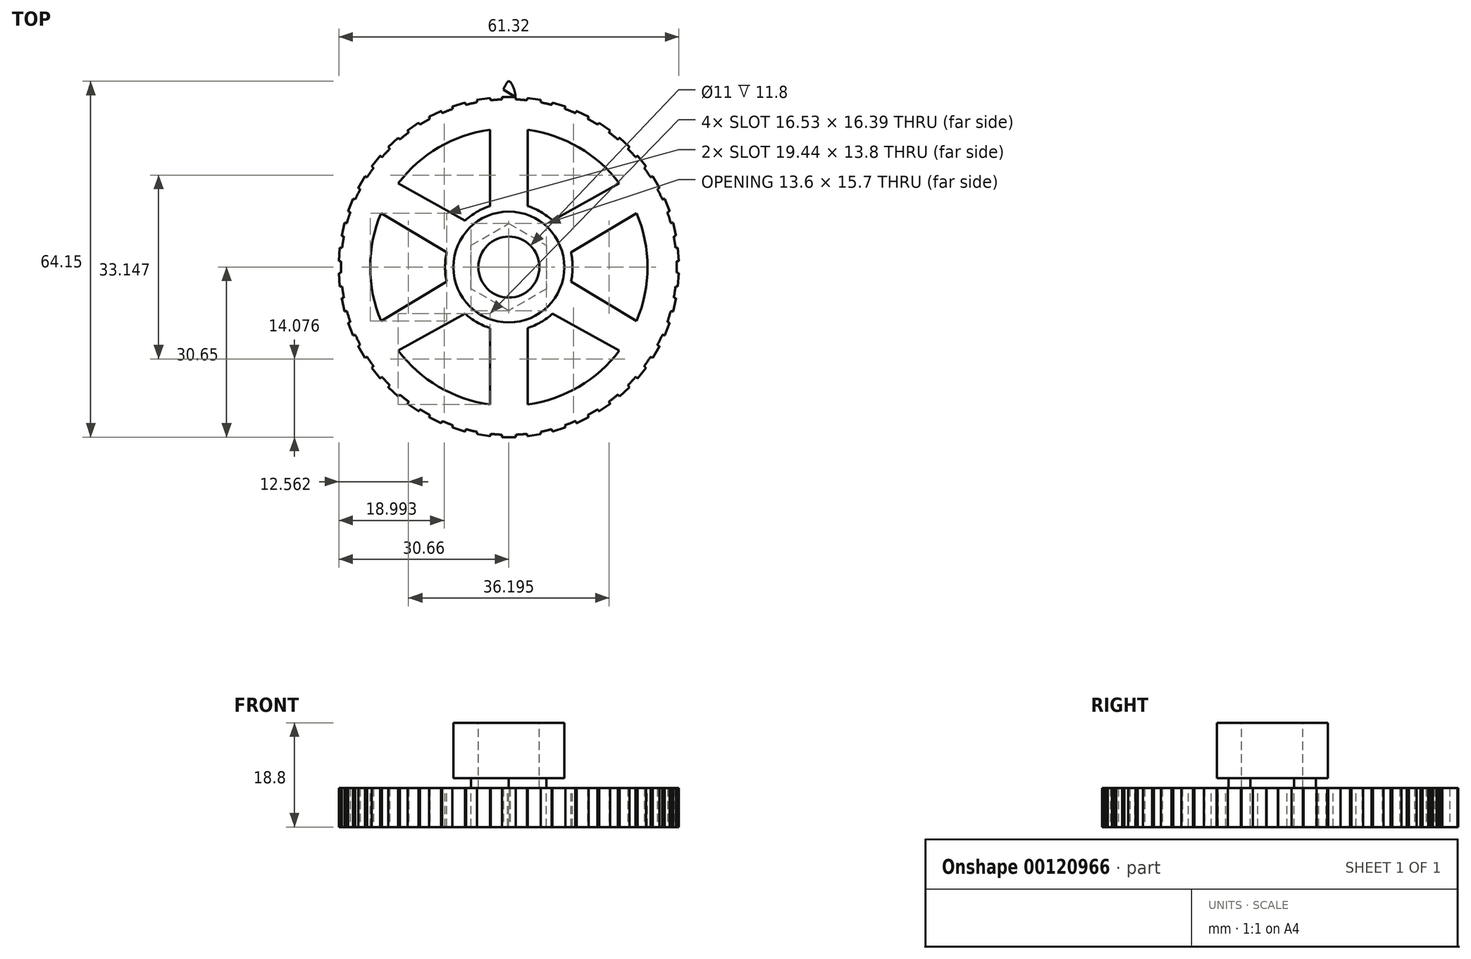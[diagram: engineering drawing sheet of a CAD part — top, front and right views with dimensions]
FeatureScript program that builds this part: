
annotation { "Feature Type Name" : "Feature", "Feature Type Description" : "" }
export const myFeature = defineFeature(function(context is Context, id is Id, definition is map)
    precondition{}
    {
        {
            var Q0;
            Q0=qCreatedBy(makeId("Top.planeOp"),FACE);
            var sketch = newSketch(context, id + "F0", { "sketchPlane" : qUnion([Q0])});
            skCircle(sketch, "E0", {"center": v(0, 0) * mm, "radius": 30 * mm});
            skCircle(sketch, "E1", {"center": v(0, 0) * mm, "radius": 33.5 * mm});
            skLineSegment(sketch, "E2", {"start": v(0, 30) * mm, "end": v(0, 33.5) * mm});
            skLineSegment(sketch, "E3", {"start": v(0, 33.5) * mm, "end": v(1.25, 33.5) * mm});
            skLineSegment(sketch, "E4", {"start": v(1.25, 33.5) * mm, "end": v(1.25, 29.64) * mm});
            skLineSegment(sketch, "E5", {"start": v(1.25, 29.64) * mm, "end": v(-1.25, 29.64) * mm});
            skLineSegment(sketch, "E6", {"start": v(-1.25, 29.64) * mm, "end": v(-1.25, 33.48) * mm});
            skLineSegment(sketch, "E7", {"start": v(-1.25, 33.48) * mm, "end": v(0, 33.5) * mm});
            skFitSpline(sketch, "E8", {"points": [v(0, 33.5) * mm, v(0.24, 33.37) * mm, v(0.97, 32) * mm, v(1.25, 29.97) * mm], "startDerivative": vector(1.35, -0.38) * mm, "endDerivative": vector(0.23, -4.54) * mm});
            skLineSegment(sketch, "E9", {"start": v(0.07, 33.48) * mm, "end": v(-0.07, 33.48) * mm});
            skLineSegment(sketch, "E10", {"start": v(-0.07, 33.48) * mm, "end": v(0.24, 33.37) * mm});
            skLineSegment(sketch, "E11", {"start": v(0.24, 33.37) * mm, "end": v(-0.24, 33.37) * mm});
            skLineSegment(sketch, "E12", {"start": v(-0.24, 33.37) * mm, "end": v(0.97, 32) * mm});
            skLineSegment(sketch, "E13", {"start": v(0.97, 32) * mm, "end": v(-0.97, 32) * mm});
            skLineSegment(sketch, "E14", {"start": v(-0.97, 32) * mm, "end": v(1.22, 30.65) * mm});
            skLineSegment(sketch, "E15", {"start": v(1.22, 30.65) * mm, "end": v(-1.21, 30.65) * mm});
            skLineSegment(sketch, "E16", {"start": v(-1.21, 30.65) * mm, "end": v(1.22, 30.65) * mm});
            skFitSpline(sketch, "E17", {"points": [v(0, 33.5) * mm, v(-0.07, 33.48) * mm, v(-0.24, 33.37) * mm, v(-0.97, 32) * mm, v(-1.21, 30.65) * mm, v(-1.25, 29.97) * mm], "startDerivative": vector(-1, -0.26) * mm, "endDerivative": vector(-0.13, -3.02) * mm});
            skSolve(sketch);
        }
        {
            var Q0;
            {var subQ0=sQuery(id+"F0.wireOp",EDGE,"E10");var subQ1=sQuery(id+"F0.wireOp",EDGE,"E2");var subQ2=makeQuery(id+"F0.imprint","INTERSECT",VERTEX,{"derivedFrom":[subQ1,subQ0]});Q0=makeQuery(id+"F0.imprint","IMPRINT",FACE,{"disambiguationData":[TD([[makeQuery(id+"F0.imprint","IMPRINT",EDGE,{"disambiguationData":[TD([[subQ2,-1.0]])],"derivedFrom":subQ1}),1.0]])]});}
            var Q1;
            {var subQ0=sQuery(id+"F0.wireOp",EDGE,"E10");var subQ1=sQuery(id+"F0.wireOp",EDGE,"E2");var subQ2=makeQuery(id+"F0.imprint","INTERSECT",VERTEX,{"derivedFrom":[subQ1,subQ0]});Q1=makeQuery(id+"F0.imprint","IMPRINT",FACE,{"disambiguationData":[TD([[makeQuery(id+"F0.imprint","IMPRINT",EDGE,{"disambiguationData":[TD([[subQ2,-1.0]])],"derivedFrom":subQ1}),-1.0]])]});}
            var Q2;
            {var subQ0=sQuery(id+"F0.wireOp",EDGE,"E11");var subQ1=sQuery(id+"F0.wireOp",EDGE,"E2");var subQ2=makeQuery(id+"F0.imprint","INTERSECT",VERTEX,{"derivedFrom":[subQ1,subQ0]});Q2=makeQuery(id+"F0.imprint","IMPRINT",FACE,{"disambiguationData":[TD([[makeQuery(id+"F0.imprint","IMPRINT",EDGE,{"disambiguationData":[TD([[subQ2,-1.0]])],"derivedFrom":subQ1}),-1.0]])]});}
            var Q3;
            {var subQ0=sQuery(id+"F0.wireOp",EDGE,"E11");var subQ1=sQuery(id+"F0.wireOp",EDGE,"E2");var subQ2=makeQuery(id+"F0.imprint","INTERSECT",VERTEX,{"derivedFrom":[subQ1,subQ0]});Q3=makeQuery(id+"F0.imprint","IMPRINT",FACE,{"disambiguationData":[TD([[makeQuery(id+"F0.imprint","IMPRINT",EDGE,{"disambiguationData":[TD([[subQ2,-1.0]])],"derivedFrom":subQ1}),1.0]])]});}
            var Q4;
            {var subQ0=sQuery(id+"F0.wireOp",EDGE,"E12");var subQ1=sQuery(id+"F0.wireOp",EDGE,"E2");var subQ2=makeQuery(id+"F0.imprint","INTERSECT",VERTEX,{"derivedFrom":[subQ1,subQ0]});Q4=makeQuery(id+"F0.imprint","IMPRINT",FACE,{"disambiguationData":[TD([[makeQuery(id+"F0.imprint","IMPRINT",EDGE,{"disambiguationData":[TD([[subQ2,-1.0]])],"derivedFrom":subQ1}),1.0]])]});}
            var Q5;
            {var subQ0=sQuery(id+"F0.wireOp",EDGE,"E12");var subQ1=sQuery(id+"F0.wireOp",EDGE,"E2");var subQ2=makeQuery(id+"F0.imprint","INTERSECT",VERTEX,{"derivedFrom":[subQ1,subQ0]});Q5=makeQuery(id+"F0.imprint","IMPRINT",FACE,{"disambiguationData":[TD([[makeQuery(id+"F0.imprint","IMPRINT",EDGE,{"disambiguationData":[TD([[subQ2,-1.0]])],"derivedFrom":subQ1}),-1.0]])]});}
            var Q6;
            {var subQ0=sQuery(id+"F0.wireOp",EDGE,"E13");var subQ1=sQuery(id+"F0.wireOp",EDGE,"E2");var subQ2=makeQuery(id+"F0.imprint","INTERSECT",VERTEX,{"derivedFrom":[subQ1,subQ0]});Q6=makeQuery(id+"F0.imprint","IMPRINT",FACE,{"disambiguationData":[TD([[makeQuery(id+"F0.imprint","IMPRINT",EDGE,{"disambiguationData":[TD([[subQ2,-1.0]])],"derivedFrom":subQ1}),1.0]])]});}
            var Q7;
            {var subQ0=sQuery(id+"F0.wireOp",EDGE,"E13");var subQ1=sQuery(id+"F0.wireOp",EDGE,"E2");var subQ2=makeQuery(id+"F0.imprint","INTERSECT",VERTEX,{"derivedFrom":[subQ1,subQ0]});Q7=makeQuery(id+"F0.imprint","IMPRINT",FACE,{"disambiguationData":[TD([[makeQuery(id+"F0.imprint","IMPRINT",EDGE,{"disambiguationData":[TD([[subQ2,-1.0]])],"derivedFrom":subQ1}),-1.0]])]});}
            var Q8;
            {var subQ0=sQuery(id+"F0.wireOp",EDGE,"E14");var subQ1=sQuery(id+"F0.wireOp",EDGE,"E2");var subQ2=makeQuery(id+"F0.imprint","INTERSECT",VERTEX,{"derivedFrom":[subQ1,subQ0]});Q8=makeQuery(id+"F0.imprint","IMPRINT",FACE,{"disambiguationData":[TD([[makeQuery(id+"F0.imprint","IMPRINT",EDGE,{"disambiguationData":[TD([[subQ2,-1.0]])],"derivedFrom":subQ1}),-1.0]])]});}
            var Q9;
            {var subQ0=sQuery(id+"F0.wireOp",EDGE,"E14");var subQ1=sQuery(id+"F0.wireOp",EDGE,"E2");var subQ2=makeQuery(id+"F0.imprint","INTERSECT",VERTEX,{"derivedFrom":[subQ1,subQ0]});Q9=makeQuery(id+"F0.imprint","IMPRINT",FACE,{"disambiguationData":[TD([[makeQuery(id+"F0.imprint","IMPRINT",EDGE,{"disambiguationData":[TD([[subQ2,-1.0]])],"derivedFrom":subQ1}),1.0]])]});}
            var Q10;
            {var subQ0=sQuery(id+"F0.wireOp",EDGE,"E16");var subQ1=sQuery(id+"F0.wireOp",EDGE,"E2");var subQ2=makeQuery(id+"F0.imprint","INTERSECT",VERTEX,{"derivedFrom":[subQ1,subQ0]});Q10=makeQuery(id+"F0.imprint","IMPRINT",FACE,{"disambiguationData":[TD([[makeQuery(id+"F0.imprint","IMPRINT",EDGE,{"disambiguationData":[TD([[subQ2,-1.0]])],"derivedFrom":subQ1}),1.0]])]});}
            var Q11;
            {var subQ0=sQuery(id+"F0.wireOp",EDGE,"E16");var subQ1=sQuery(id+"F0.wireOp",EDGE,"E2");var subQ2=makeQuery(id+"F0.imprint","INTERSECT",VERTEX,{"derivedFrom":[subQ1,subQ0]});Q11=makeQuery(id+"F0.imprint","IMPRINT",FACE,{"disambiguationData":[TD([[makeQuery(id+"F0.imprint","IMPRINT",EDGE,{"disambiguationData":[TD([[subQ2,-1.0]])],"derivedFrom":subQ1}),-1.0]])]});}
            var Q12;
            {var subQ0=sQuery(id+"F0.wireOp",EDGE,"E2");var subQ1=sQuery(id+"F0.wireOp",EDGE,"E0");var subQ2=makeQuery(id+"F0.imprint","INTERSECT",VERTEX,{"derivedFrom":[subQ1,subQ0]});Q12=makeQuery(id+"F0.imprint","IMPRINT",FACE,{"disambiguationData":[TD([[makeQuery(id+"F0.imprint","IMPRINT",EDGE,{"disambiguationData":[TD([[subQ2,-1.0]])],"derivedFrom":subQ0}),-1.0]])]});}
            var Q13;
            {var subQ0=sQuery(id+"F0.wireOp",EDGE,"E2");var subQ1=sQuery(id+"F0.wireOp",EDGE,"E0");var subQ2=makeQuery(id+"F0.imprint","INTERSECT",VERTEX,{"derivedFrom":[subQ1,subQ0]});Q13=makeQuery(id+"F0.imprint","IMPRINT",FACE,{"disambiguationData":[TD([[makeQuery(id+"F0.imprint","IMPRINT",EDGE,{"disambiguationData":[TD([[subQ2,-1.0]])],"derivedFrom":subQ0}),1.0]])]});}
            extrude(context, id + "F1", {"entities" : qUnion([Q0, Q1, Q2, Q3, Q4, Q5, Q6, Q7, Q8, Q9, Q10, Q11, Q12, Q13]), "depth" : 7 * mm});
        }
        {
            var Q0;
            Q0=qCreatedBy(makeId("Top.planeOp"),FACE);
            var sketch = newSketch(context, id + "F2", { "sketchPlane" : qUnion([Q0])});
            skCircle(sketch, "E18", {"center": v(0, 0) * mm, "radius": 4.18 * mm});
            skSolve(sketch);
        }
        {
            var Q0;
            Q0 = qSketchRegion(id + "F2", true);
            extrude(context, id + "F3", {"entities" : qUnion([Q0]), "depth" : 25 * mm});
        }
        {
            var Q0;
            Q0=makeQuery(id+"F1.opExtrude","SWEPT_BODY",BODY,{"disambiguationData":[OSD([sQuery(id+"F0.wireOp",EDGE,"E0"),sQuery(id+"F0.wireOp",EDGE,"E8"),sQuery(id+"F0.wireOp",EDGE,"E9"),sQuery(id+"F0.wireOp",EDGE,"E17")])]});
            var Q1;
            Q1=makeQuery(id+"F3.opExtrude","CAP_EDGE",EDGE,{"disambiguationData":[OSD([sQuery(id+"F2.wireOp",EDGE,"E18")])],"isStart":false});
            circularPattern(context, id + "F4", {"entities" : qUnion([Q0]), "axis" : qUnion([Q1]), "angle" : 360 * degree, "instanceCount" : 42, "equalSpace" : true});
        }
        {
            var Q0;
            Q0=makeQuery(id+"F3.opExtrude","CAP_FACE",FACE,{"disambiguationData":[OSD([sQuery(id+"F2.wireOp",EDGE,"E18")])],"isStart":false});
            var sketch = newSketch(context, id + "F5", { "sketchPlane" : qUnion([Q0])});
            skCircle(sketch, "E19", {"center": v(0, 0) * mm, "radius": 6.48 * mm});
            skSolve(sketch);
        }
        {
            var Q0;
            Q0 = qSketchRegion(id + "F5", true);
            extrude(context, id + "F6", {"entities" : qUnion([Q0]), "operationType" : NewBodyOperationType.REMOVE, "oppositeDirection" : true, "depth" : 25 * mm});
        }
        {
            var Q0;
            Q0=qCreatedBy(makeId("Top.planeOp"),FACE);
            var sketch = newSketch(context, id + "F7", { "sketchPlane" : qUnion([Q0])});
            skCircle(sketch, "E20", {"center": v(0, 0) * mm, "radius": 30.25 * mm});
            skSolve(sketch);
        }
        {
            var Q0;
            Q0=makeQuery(id+"F7.imprint","IMPRINT",FACE,{"disambiguationData":[TD([[makeQuery(id+"F7.imprint","IMPRINT",EDGE,{"derivedFrom":sQuery(id+"F7.wireOp",EDGE,"E20")}),1.0]])]});
            extrude(context, id + "F8", {"entities" : qUnion([Q0]), "operationType" : NewBodyOperationType.ADD, "depth" : 7 * mm});
        }
        {
            var Q0;
            {var subQ0=makeQuery(id+"F1.opExtrude","CAP_FACE",FACE,{"disambiguationData":[OSD([sQuery(id+"F0.wireOp",EDGE,"E0"),sQuery(id+"F0.wireOp",EDGE,"E8"),sQuery(id+"F0.wireOp",EDGE,"E9"),sQuery(id+"F0.wireOp",EDGE,"E17")])],"isStart":false});Q0=makeQuery(id+"F8.boolean.opBoolean","MERGE",FACE,{"derivedFrom":[subQ0,makeQuery(id+"F4.opPattern","COPY",FACE,{"derivedFrom":subQ0,"instanceName":"1"}),makeQuery(id+"F4.opPattern","COPY",FACE,{"derivedFrom":subQ0,"instanceName":"2"}),makeQuery(id+"F4.opPattern","COPY",FACE,{"derivedFrom":subQ0,"instanceName":"3"}),makeQuery(id+"F4.opPattern","COPY",FACE,{"derivedFrom":subQ0,"instanceName":"4"}),makeQuery(id+"F4.opPattern","COPY",FACE,{"derivedFrom":subQ0,"instanceName":"5"}),makeQuery(id+"F4.opPattern","COPY",FACE,{"derivedFrom":subQ0,"instanceName":"6"}),makeQuery(id+"F4.opPattern","COPY",FACE,{"derivedFrom":subQ0,"instanceName":"7"}),makeQuery(id+"F4.opPattern","COPY",FACE,{"derivedFrom":subQ0,"instanceName":"8"}),makeQuery(id+"F4.opPattern","COPY",FACE,{"derivedFrom":subQ0,"instanceName":"9"}),makeQuery(id+"F4.opPattern","COPY",FACE,{"derivedFrom":subQ0,"instanceName":"10"}),makeQuery(id+"F4.opPattern","COPY",FACE,{"derivedFrom":subQ0,"instanceName":"11"}),makeQuery(id+"F4.opPattern","COPY",FACE,{"derivedFrom":subQ0,"instanceName":"12"}),makeQuery(id+"F4.opPattern","COPY",FACE,{"derivedFrom":subQ0,"instanceName":"13"}),makeQuery(id+"F4.opPattern","COPY",FACE,{"derivedFrom":subQ0,"instanceName":"14"}),makeQuery(id+"F4.opPattern","COPY",FACE,{"derivedFrom":subQ0,"instanceName":"15"}),makeQuery(id+"F4.opPattern","COPY",FACE,{"derivedFrom":subQ0,"instanceName":"16"}),makeQuery(id+"F4.opPattern","COPY",FACE,{"derivedFrom":subQ0,"instanceName":"17"}),makeQuery(id+"F4.opPattern","COPY",FACE,{"derivedFrom":subQ0,"instanceName":"18"}),makeQuery(id+"F4.opPattern","COPY",FACE,{"derivedFrom":subQ0,"instanceName":"19"}),makeQuery(id+"F4.opPattern","COPY",FACE,{"derivedFrom":subQ0,"instanceName":"20"}),makeQuery(id+"F4.opPattern","COPY",FACE,{"derivedFrom":subQ0,"instanceName":"21"}),makeQuery(id+"F4.opPattern","COPY",FACE,{"derivedFrom":subQ0,"instanceName":"22"}),makeQuery(id+"F4.opPattern","COPY",FACE,{"derivedFrom":subQ0,"instanceName":"23"}),makeQuery(id+"F4.opPattern","COPY",FACE,{"derivedFrom":subQ0,"instanceName":"24"}),makeQuery(id+"F4.opPattern","COPY",FACE,{"derivedFrom":subQ0,"instanceName":"25"}),makeQuery(id+"F4.opPattern","COPY",FACE,{"derivedFrom":subQ0,"instanceName":"26"}),makeQuery(id+"F4.opPattern","COPY",FACE,{"derivedFrom":subQ0,"instanceName":"27"}),makeQuery(id+"F4.opPattern","COPY",FACE,{"derivedFrom":subQ0,"instanceName":"28"}),makeQuery(id+"F4.opPattern","COPY",FACE,{"derivedFrom":subQ0,"instanceName":"29"}),makeQuery(id+"F4.opPattern","COPY",FACE,{"derivedFrom":subQ0,"instanceName":"30"}),makeQuery(id+"F4.opPattern","COPY",FACE,{"derivedFrom":subQ0,"instanceName":"31"}),makeQuery(id+"F4.opPattern","COPY",FACE,{"derivedFrom":subQ0,"instanceName":"32"}),makeQuery(id+"F4.opPattern","COPY",FACE,{"derivedFrom":subQ0,"instanceName":"33"}),makeQuery(id+"F4.opPattern","COPY",FACE,{"derivedFrom":subQ0,"instanceName":"34"}),makeQuery(id+"F4.opPattern","COPY",FACE,{"derivedFrom":subQ0,"instanceName":"35"}),makeQuery(id+"F4.opPattern","COPY",FACE,{"derivedFrom":subQ0,"instanceName":"36"}),makeQuery(id+"F4.opPattern","COPY",FACE,{"derivedFrom":subQ0,"instanceName":"37"}),makeQuery(id+"F4.opPattern","COPY",FACE,{"derivedFrom":subQ0,"instanceName":"38"}),makeQuery(id+"F4.opPattern","COPY",FACE,{"derivedFrom":subQ0,"instanceName":"39"}),makeQuery(id+"F4.opPattern","COPY",FACE,{"derivedFrom":subQ0,"instanceName":"40"}),makeQuery(id+"F4.opPattern","COPY",FACE,{"derivedFrom":subQ0,"instanceName":"41"}),makeQuery(id+"F4.opPattern","COPY",FACE,{"derivedFrom":subQ0,"instanceName":"42"}),makeQuery(id+"F4.opPattern","COPY",FACE,{"derivedFrom":subQ0,"instanceName":"43"}),makeQuery(id+"F4.opPattern","COPY",FACE,{"derivedFrom":subQ0,"instanceName":"44"}),makeQuery(id+"F4.opPattern","COPY",FACE,{"derivedFrom":subQ0,"instanceName":"45"}),makeQuery(id+"F4.opPattern","COPY",FACE,{"derivedFrom":subQ0,"instanceName":"46"}),makeQuery(id+"F4.opPattern","COPY",FACE,{"derivedFrom":subQ0,"instanceName":"47"}),makeQuery(id+"F4.opPattern","COPY",FACE,{"derivedFrom":subQ0,"instanceName":"48"}),makeQuery(id+"F4.opPattern","COPY",FACE,{"derivedFrom":subQ0,"instanceName":"49"}),makeQuery(id+"F4.opPattern","COPY",FACE,{"derivedFrom":subQ0,"instanceName":"50"}),makeQuery(id+"F4.opPattern","COPY",FACE,{"derivedFrom":subQ0,"instanceName":"51"}),makeQuery(id+"F4.opPattern","COPY",FACE,{"derivedFrom":subQ0,"instanceName":"52"}),makeQuery(id+"F4.opPattern","COPY",FACE,{"derivedFrom":subQ0,"instanceName":"53"}),makeQuery(id+"F8.opExtrude","CAP_FACE",FACE,{"disambiguationData":[OSD([sQuery(id+"F7.wireOp",EDGE,"E20")])],"isStart":false})]});}
            var sketch = newSketch(context, id + "F9", { "sketchPlane" : qUnion([Q0])});
            skLineSegment(sketch, "E21", {"start": v(0, 0) * mm, "end": v(6.8, 0) * mm});
            skCircle(sketch, "E22.cCircle", {"center": v(0, 0) * mm, "radius": 6.8 * mm, "construction": true});
            skLineSegment(sketch, "E22.0", {"start": v(6.8, 3.93) * mm, "end": v(6.8, -3.93) * mm});
            skLineSegment(sketch, "E22.1", {"start": v(6.8, -3.93) * mm, "end": v(0, -7.85) * mm});
            skLineSegment(sketch, "E22.2", {"start": v(0, -7.85) * mm, "end": v(-6.8, -3.93) * mm});
            skLineSegment(sketch, "E22.3", {"start": v(-6.8, -3.93) * mm, "end": v(-6.8, 3.93) * mm});
            skLineSegment(sketch, "E22.4", {"start": v(-6.8, 3.93) * mm, "end": v(0, 7.85) * mm});
            skLineSegment(sketch, "E22.5", {"start": v(0, 7.85) * mm, "end": v(6.8, 3.93) * mm});
            skPoint(sketch, "E22.0.midPoint", {"position": v(6.8, 0) * mm});
            skCircle(sketch, "E23", {"center": v(0, 0) * mm, "radius": 25 * mm});
            skCircle(sketch, "E24.cCircle", {"center": v(0, 0) * mm, "radius": 25.74 * mm, "construction": true});
            skCircle(sketch, "E25", {"center": v(0, 0) * mm, "radius": 11.5 * mm});
            skLineSegment(sketch, "E26", {"start": v(6.8, 0) * mm, "end": v(23.67, 10.1) * mm});
            skLineSegment(sketch, "E27", {"start": v(3.4, 5.89) * mm, "end": v(20.58, 15.45) * mm});
            skLineSegment(sketch, "E28", {"start": v(3.4, 5.89) * mm, "end": v(3.4, 25.51) * mm});
            skLineSegment(sketch, "E29", {"start": v(-3.4, 5.89) * mm, "end": v(-3.4, 25.51) * mm});
            skLineSegment(sketch, "E30", {"start": v(-3.4, -5.89) * mm, "end": v(-3.4, -25.51) * mm});
            skLineSegment(sketch, "E31", {"start": v(3.4, -5.89) * mm, "end": v(3.4, -25.51) * mm});
            skLineSegment(sketch, "E32", {"start": v(3.4, -5.89) * mm, "end": v(20.58, -15.45) * mm});
            skLineSegment(sketch, "E33", {"start": v(6.8, 0) * mm, "end": v(23.67, -10.1) * mm});
            skLineSegment(sketch, "E34", {"start": v(-3.4, -5.89) * mm, "end": v(-20.58, -15.45) * mm});
            skLineSegment(sketch, "E35", {"start": v(-6.8, 0) * mm, "end": v(-23.67, -10.1) * mm});
            skLineSegment(sketch, "E36", {"start": v(-3.4, 5.89) * mm, "end": v(-20.58, 15.45) * mm});
            skLineSegment(sketch, "E37", {"start": v(-6.8, 0) * mm, "end": v(-23.67, 10.1) * mm});
            skSolve(sketch);
        }
        {
            var Q0;
            {var subQ0=sQuery(id+"F9.wireOp",EDGE,"E27");var subQ1=sQuery(id+"F9.wireOp",EDGE,"E23");var subQ2=makeQuery(id+"F9.imprint","INTERSECT",VERTEX,{"derivedFrom":[subQ1,subQ0]});Q0=makeQuery(id+"F9.imprint","IMPRINT",FACE,{"disambiguationData":[TD([[makeQuery(id+"F9.imprint","IMPRINT",EDGE,{"disambiguationData":[TD([[subQ2,-1.0]])],"derivedFrom":subQ1}),1.0]])]});}
            var Q1;
            {var subQ0=sQuery(id+"F9.wireOp",EDGE,"E29");var subQ1=sQuery(id+"F9.wireOp",EDGE,"E23");var subQ2=makeQuery(id+"F9.imprint","INTERSECT",VERTEX,{"derivedFrom":[subQ1,subQ0]});Q1=makeQuery(id+"F9.imprint","IMPRINT",FACE,{"disambiguationData":[TD([[makeQuery(id+"F9.imprint","IMPRINT",EDGE,{"disambiguationData":[TD([[subQ2,-1.0]])],"derivedFrom":subQ1}),1.0]])]});}
            var Q2;
            {var subQ0=sQuery(id+"F9.wireOp",EDGE,"E35");var subQ1=sQuery(id+"F9.wireOp",EDGE,"E23");var subQ2=makeQuery(id+"F9.imprint","INTERSECT",VERTEX,{"derivedFrom":[subQ1,subQ0]});Q2=makeQuery(id+"F9.imprint","IMPRINT",FACE,{"disambiguationData":[TD([[makeQuery(id+"F9.imprint","IMPRINT",EDGE,{"disambiguationData":[TD([[subQ2,1.0]])],"derivedFrom":subQ1}),1.0]])]});}
            var Q3;
            {var subQ0=sQuery(id+"F9.wireOp",EDGE,"E30");var subQ1=sQuery(id+"F9.wireOp",EDGE,"E23");var subQ2=makeQuery(id+"F9.imprint","INTERSECT",VERTEX,{"derivedFrom":[subQ1,subQ0]});Q3=makeQuery(id+"F9.imprint","IMPRINT",FACE,{"disambiguationData":[TD([[makeQuery(id+"F9.imprint","IMPRINT",EDGE,{"disambiguationData":[TD([[subQ2,1.0]])],"derivedFrom":subQ1}),1.0]])]});}
            var Q4;
            {var subQ0=sQuery(id+"F9.wireOp",EDGE,"E31");var subQ1=sQuery(id+"F9.wireOp",EDGE,"E23");var subQ2=makeQuery(id+"F9.imprint","INTERSECT",VERTEX,{"derivedFrom":[subQ1,subQ0]});Q4=makeQuery(id+"F9.imprint","IMPRINT",FACE,{"disambiguationData":[TD([[makeQuery(id+"F9.imprint","IMPRINT",EDGE,{"disambiguationData":[TD([[subQ2,-1.0]])],"derivedFrom":subQ1}),1.0]])]});}
            var Q5;
            {var subQ0=sQuery(id+"F9.wireOp",EDGE,"E22.5");var subQ11=sQuery(id+"F9.wireOp",EDGE,"E22.0");var subQ16=makeQuery(id+"F9.imprint","INTERSECT",VERTEX,{"derivedFrom":[subQ11,subQ0]});Q5=makeQuery(id+"F9.imprint","IMPRINT",FACE,{"disambiguationData":[TD([[makeQuery(id+"F9.imprint","IMPRINT",EDGE,{"disambiguationData":[TD([[subQ16,-1.0]])],"derivedFrom":subQ11}),-1.0]])]});}
            var Q6;
            {var subQ0=sQuery(id+"F9.wireOp",EDGE,"E26");var subQ1=sQuery(id+"F9.wireOp",EDGE,"E23");var subQ2=makeQuery(id+"F9.imprint","INTERSECT",VERTEX,{"derivedFrom":[subQ1,subQ0]});Q6=makeQuery(id+"F9.imprint","IMPRINT",FACE,{"disambiguationData":[TD([[makeQuery(id+"F9.imprint","IMPRINT",EDGE,{"disambiguationData":[TD([[subQ2,1.0]])],"derivedFrom":subQ1}),1.0]])]});}
            extrude(context, id + "F10", {"entities" : qUnion([Q0, Q1, Q2, Q3, Q4, Q5, Q6]), "operationType" : NewBodyOperationType.REMOVE, "oppositeDirection" : true, "depth" : 25 * mm});
        }
        {
            var Q0;
            {var subQ0=makeQuery(id+"F1.opExtrude","CAP_FACE",FACE,{"disambiguationData":[OSD([sQuery(id+"F0.wireOp",EDGE,"E0"),sQuery(id+"F0.wireOp",EDGE,"E8"),sQuery(id+"F0.wireOp",EDGE,"E9"),sQuery(id+"F0.wireOp",EDGE,"E17")])],"isStart":false});Q0=makeQuery(id+"F8.boolean.opBoolean","MERGE",FACE,{"derivedFrom":[subQ0,makeQuery(id+"F4.opPattern","COPY",FACE,{"derivedFrom":subQ0,"instanceName":"1"}),makeQuery(id+"F4.opPattern","COPY",FACE,{"derivedFrom":subQ0,"instanceName":"2"}),makeQuery(id+"F4.opPattern","COPY",FACE,{"derivedFrom":subQ0,"instanceName":"3"}),makeQuery(id+"F4.opPattern","COPY",FACE,{"derivedFrom":subQ0,"instanceName":"4"}),makeQuery(id+"F4.opPattern","COPY",FACE,{"derivedFrom":subQ0,"instanceName":"5"}),makeQuery(id+"F4.opPattern","COPY",FACE,{"derivedFrom":subQ0,"instanceName":"6"}),makeQuery(id+"F4.opPattern","COPY",FACE,{"derivedFrom":subQ0,"instanceName":"7"}),makeQuery(id+"F4.opPattern","COPY",FACE,{"derivedFrom":subQ0,"instanceName":"8"}),makeQuery(id+"F4.opPattern","COPY",FACE,{"derivedFrom":subQ0,"instanceName":"9"}),makeQuery(id+"F4.opPattern","COPY",FACE,{"derivedFrom":subQ0,"instanceName":"10"}),makeQuery(id+"F4.opPattern","COPY",FACE,{"derivedFrom":subQ0,"instanceName":"11"}),makeQuery(id+"F4.opPattern","COPY",FACE,{"derivedFrom":subQ0,"instanceName":"12"}),makeQuery(id+"F4.opPattern","COPY",FACE,{"derivedFrom":subQ0,"instanceName":"13"}),makeQuery(id+"F4.opPattern","COPY",FACE,{"derivedFrom":subQ0,"instanceName":"14"}),makeQuery(id+"F4.opPattern","COPY",FACE,{"derivedFrom":subQ0,"instanceName":"15"}),makeQuery(id+"F4.opPattern","COPY",FACE,{"derivedFrom":subQ0,"instanceName":"16"}),makeQuery(id+"F4.opPattern","COPY",FACE,{"derivedFrom":subQ0,"instanceName":"17"}),makeQuery(id+"F4.opPattern","COPY",FACE,{"derivedFrom":subQ0,"instanceName":"18"}),makeQuery(id+"F4.opPattern","COPY",FACE,{"derivedFrom":subQ0,"instanceName":"19"}),makeQuery(id+"F4.opPattern","COPY",FACE,{"derivedFrom":subQ0,"instanceName":"20"}),makeQuery(id+"F4.opPattern","COPY",FACE,{"derivedFrom":subQ0,"instanceName":"21"}),makeQuery(id+"F4.opPattern","COPY",FACE,{"derivedFrom":subQ0,"instanceName":"22"}),makeQuery(id+"F4.opPattern","COPY",FACE,{"derivedFrom":subQ0,"instanceName":"23"}),makeQuery(id+"F4.opPattern","COPY",FACE,{"derivedFrom":subQ0,"instanceName":"24"}),makeQuery(id+"F4.opPattern","COPY",FACE,{"derivedFrom":subQ0,"instanceName":"25"}),makeQuery(id+"F4.opPattern","COPY",FACE,{"derivedFrom":subQ0,"instanceName":"26"}),makeQuery(id+"F4.opPattern","COPY",FACE,{"derivedFrom":subQ0,"instanceName":"27"}),makeQuery(id+"F4.opPattern","COPY",FACE,{"derivedFrom":subQ0,"instanceName":"28"}),makeQuery(id+"F4.opPattern","COPY",FACE,{"derivedFrom":subQ0,"instanceName":"29"}),makeQuery(id+"F4.opPattern","COPY",FACE,{"derivedFrom":subQ0,"instanceName":"30"}),makeQuery(id+"F4.opPattern","COPY",FACE,{"derivedFrom":subQ0,"instanceName":"31"}),makeQuery(id+"F4.opPattern","COPY",FACE,{"derivedFrom":subQ0,"instanceName":"32"}),makeQuery(id+"F4.opPattern","COPY",FACE,{"derivedFrom":subQ0,"instanceName":"33"}),makeQuery(id+"F4.opPattern","COPY",FACE,{"derivedFrom":subQ0,"instanceName":"34"}),makeQuery(id+"F4.opPattern","COPY",FACE,{"derivedFrom":subQ0,"instanceName":"35"}),makeQuery(id+"F4.opPattern","COPY",FACE,{"derivedFrom":subQ0,"instanceName":"36"}),makeQuery(id+"F4.opPattern","COPY",FACE,{"derivedFrom":subQ0,"instanceName":"37"}),makeQuery(id+"F4.opPattern","COPY",FACE,{"derivedFrom":subQ0,"instanceName":"38"}),makeQuery(id+"F4.opPattern","COPY",FACE,{"derivedFrom":subQ0,"instanceName":"39"}),makeQuery(id+"F4.opPattern","COPY",FACE,{"derivedFrom":subQ0,"instanceName":"40"}),makeQuery(id+"F4.opPattern","COPY",FACE,{"derivedFrom":subQ0,"instanceName":"41"}),makeQuery(id+"F8.opExtrude","CAP_FACE",FACE,{"disambiguationData":[OSD([sQuery(id+"F7.wireOp",EDGE,"E20")])],"isStart":false})]});}
            var sketch = newSketch(context, id + "F11", { "sketchPlane" : qUnion([Q0])});
            skCircle(sketch, "E38", {"center": v(0, 0) * mm, "radius": 11.5 * mm});
            skCircle(sketch, "E39", {"center": v(0, 0) * mm, "radius": 5 * mm});
            skSolve(sketch);
        }
        {
            var Q0;
            Q0=makeQuery(id+"F11.imprint","IMPRINT",FACE,{"disambiguationData":[TD([[makeQuery(id+"F11.imprint","IMPRINT",EDGE,{"derivedFrom":makeQuery(id+"F10.boolean.opBoolean","COPY",EDGE,{"derivedFrom":makeQuery(id+"F10.opExtrude","CAP_EDGE",EDGE,{"disambiguationData":[OSD([sQuery(id+"F9.wireOp",EDGE,"E22.0")])],"isStart":true})})}),1.0]])]});
            var Q1;
            Q1=makeQuery(id+"F11.imprint","IMPRINT",FACE,{"disambiguationData":[TD([[makeQuery(id+"F11.imprint","IMPRINT",EDGE,{"derivedFrom":sQuery(id+"F11.wireOp",EDGE,"E39")}),-1.0]])]});
            extrude(context, id + "F12", {"entities" : qUnion([Q0, Q1]), "operationType" : NewBodyOperationType.ADD, "depth" : 1.8 * mm});
        }
        {
            var Q0;
            Q0=makeQuery(id+"F12.opExtrude","CAP_FACE",FACE,{"disambiguationData":[OSD([sQuery(id+"F11.wireOp",EDGE,"E38"),sQuery(id+"F11.wireOp",EDGE,"E39")])],"isStart":false});
            var sketch = newSketch(context, id + "F13", { "sketchPlane" : qUnion([Q0])});
            skCircle(sketch, "E40", {"center": v(0, 0) * mm, "radius": 5.02 * mm});
            skCircle(sketch, "E41", {"center": v(0, 0) * mm, "radius": 9.9 * mm});
            skSolve(sketch);
        }
        {
            var Q0;
            Q0=makeQuery(id+"F13.imprint","IMPRINT",FACE,{"disambiguationData":[TD([[makeQuery(id+"F13.imprint","IMPRINT",EDGE,{"derivedFrom":sQuery(id+"F13.wireOp",EDGE,"E40")}),-1.0]])]});
            extrude(context, id + "F14", {"entities" : qUnion([Q0]), "operationType" : NewBodyOperationType.ADD, "depth" : 10 * mm});
        }
        {
            var Q0;
            {var subQ1=sQuery(id+"F11.wireOp",EDGE,"E38");Q0=makeQuery(id+"F14.boolean.opBoolean","SPLIT",FACE,{"disambiguationData":[TD([makeQuery(id+"F12.opExtrude","SWEPT_FACE",FACE,{"disambiguationData":[OSD([subQ1])]})])],"derivedFrom":makeQuery(id+"F12.opExtrude","CAP_FACE",FACE,{"disambiguationData":[OSD([subQ1,sQuery(id+"F11.wireOp",EDGE,"E39")])],"isStart":false})});}
            var sketch = newSketch(context, id + "F15", { "sketchPlane" : qUnion([Q0])});
            skCircle(sketch, "E42", {"center": v(0, 0) * mm, "radius": 10.7 * mm});
            skSolve(sketch);
        }
        {
            var Q0;
            Q0=makeQuery(id+"F15.imprint","IMPRINT",FACE,{"disambiguationData":[TD([[makeQuery(id+"F15.imprint","IMPRINT",EDGE,{"derivedFrom":sQuery(id+"F15.wireOp",EDGE,"E42")}),1.0]])]});
            extrude(context, id + "F16", {"entities" : qUnion([Q0]), "operationType" : NewBodyOperationType.ADD, "depth" : 10 * mm});
        }
        {
            var Q0;
            {var subQ0=sQuery(id+"F13.wireOp",EDGE,"E41");Q0=makeQuery(id+"F16.boolean.opBoolean","MERGE",FACE,{"derivedFrom":[makeQuery(id+"F14.opExtrude","CAP_FACE",FACE,{"disambiguationData":[OSD([sQuery(id+"F13.wireOp",EDGE,"E40"),subQ0])],"isStart":false}),makeQuery(id+"F16.opExtrude","CAP_FACE",FACE,{"disambiguationData":[OSD([subQ0,sQuery(id+"F15.wireOp",EDGE,"E42")])],"isStart":false})]});}
            var sketch = newSketch(context, id + "F17", { "sketchPlane" : qUnion([Q0])});
            skCircle(sketch, "E43", {"center": v(0, 0) * mm, "radius": 10 * mm});
            skCircle(sketch, "E44", {"center": v(0, 0) * mm, "radius": 5.5 * mm});
            skCircle(sketch, "E45", {"center": v(0, 0) * mm, "radius": 12.38 * mm});
            skSolve(sketch);
        }
        {
            var Q0;
            Q0 = qSketchRegion(id + "F17", true);
            var Q1;
            {var subQ1=sQuery(id+"F11.wireOp",EDGE,"E38");Q1=makeQuery(id+"F14.boolean.opBoolean","SPLIT",FACE,{"disambiguationData":[TD([makeQuery(id+"F12.opExtrude","SWEPT_FACE",FACE,{"disambiguationData":[OSD([subQ1])]})])],"derivedFrom":makeQuery(id+"F12.opExtrude","CAP_FACE",FACE,{"disambiguationData":[OSD([subQ1,sQuery(id+"F11.wireOp",EDGE,"E39")])],"isStart":false})});}
            extrude(context, id + "F18", {"entities" : qUnion([Q0]), "operationType" : NewBodyOperationType.REMOVE, "endBound" : BoundingType.UP_TO_SURFACE, "oppositeDirection" : true, "endBoundEntityFace" : qUnion([Q1]), "depth" : 25 * mm});
        }
        {
            var Q0;
            Q0=makeQuery(id+"F17.imprint","IMPRINT",FACE,{"disambiguationData":[TD([[makeQuery(id+"F17.imprint","IMPRINT",EDGE,{"derivedFrom":sQuery(id+"F17.wireOp",EDGE,"E44")}),1.0]])]});
            var Q1;
            Q1=makeQuery(id+"F17.imprint","IMPRINT",FACE,{"disambiguationData":[TD([[makeQuery(id+"F17.imprint","IMPRINT",EDGE,{"derivedFrom":makeQuery(id+"F14.opExtrude","CAP_EDGE",EDGE,{"disambiguationData":[OSD([sQuery(id+"F13.wireOp",EDGE,"E40")])],"isStart":false})}),1.0]])]});
            extrude(context, id + "F19", {"entities" : qUnion([Q0, Q1]), "operationType" : NewBodyOperationType.REMOVE, "oppositeDirection" : true, "depth" : 91.7 * mm});
        }
    });
